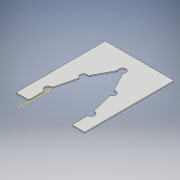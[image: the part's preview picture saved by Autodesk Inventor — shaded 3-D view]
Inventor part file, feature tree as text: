
AUTODESK INVENTOR PART (.ipt)
format: ipt  version: 2018 (Build 220112000, 112)  size: 207,360 bytes
history: native  units: mm
features: reference x11, other x4, plane x1, sheet_metal_op x1, sketch x1
ambient origin geometry x8: Origin, YZ Plane, XZ Plane, XY Plane, X Axis, Y Axis, Z Axis, Center Point
bodies: Solid1 (feature_tree)
feature tree (18):
  plane  "Work Plane1"
  sheet_metal_op  "Face1"
  sketch  "Sketch1"  dims[d0=200.0mm d1=100.0mm d2=260.0mm d3=50.0mm d4=10.0mm d5=10.0mm d6=10.0mm d7=10.0mm d8=10.0mm d9=3.0mm d10=3.0mm]
  reference  "Reference12"
  reference  "Reference13"
  reference  "Reference14"
  reference  "Reference15"
  reference  "Reference16"
  reference  "Reference17"
  reference  "Reference18"
  reference  "Reference19"
  reference  "Reference20"
  reference  "Reference21"
  reference  "Reference22"
  other  "Plate1"
  other  "Assembly1"
  other  "plade:1"
  other  "Definition1"
